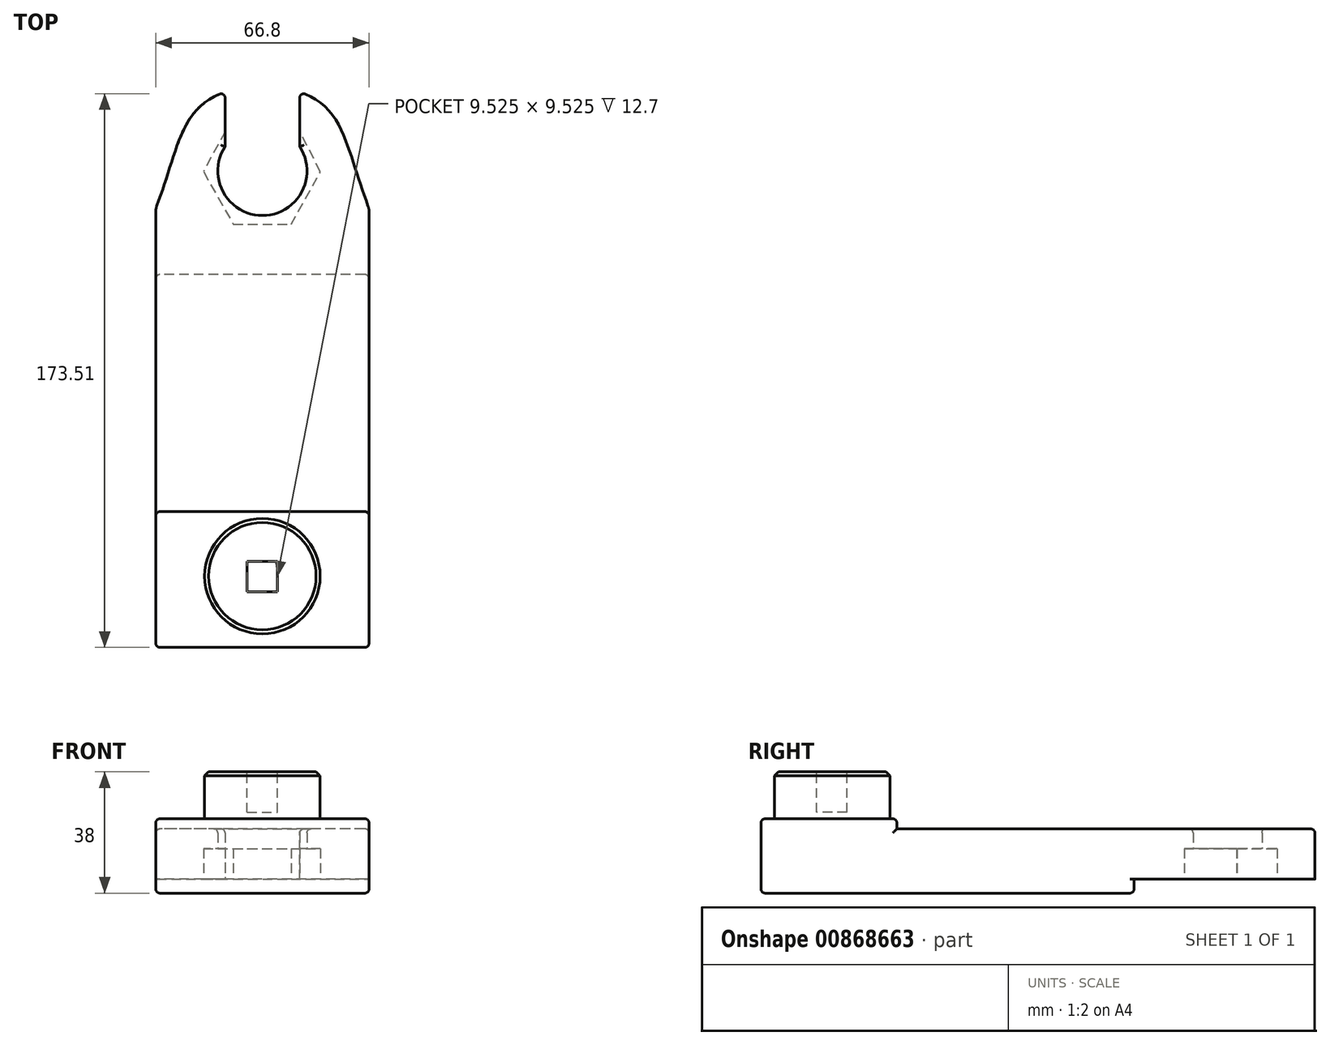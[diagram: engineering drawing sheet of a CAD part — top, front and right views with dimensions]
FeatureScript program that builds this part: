
annotation { "Feature Type Name" : "Feature", "Feature Type Description" : "" }
export const myFeature = defineFeature(function(context is Context, id is Id, definition is map)
    precondition{}
    {
        {
            var Q0;
            Q0=qCreatedBy(makeId("Top.planeOp"),FACE);
            var sketch = newSketch(context, id + "F0", { "sketchPlane" : qUnion([Q0])});
            skPoint(sketch, "E0", {"position": v(-184.46, 218.06) * mm});
            skPoint(sketch, "E1", {"position": v(-161.09, 218.06) * mm});
            skLineSegment(sketch, "E2", {"start": v(-139.37, 181.48) * mm, "end": v(-139.37, 43.95) * mm});
            skLineSegment(sketch, "E3", {"start": v(-139.37, 43.95) * mm, "end": v(-206.17, 43.95) * mm});
            skLineSegment(sketch, "E4", {"start": v(-206.17, 43.95) * mm, "end": v(-206.17, 181.48) * mm});
            skArc(sketch, "E5", {"start": v(-184.46, 200.95) * mm, "mid": v(-172.77, 179.32) * mm, "end": v(-161.09, 200.95) * mm});
            skFitSpline(sketch, "E6", {"points": [v(-206.17, 181.48) * mm, v(-184.46, 218.06) * mm], "startDerivative": vector(22.63, 60.05) * mm, "endDerivative": vector(42.75, 15.43) * mm});
            skFitSpline(sketch, "E7", {"points": [v(-161.09, 218.06) * mm, v(-139.37, 181.48) * mm], "startDerivative": vector(42.75, -15.43) * mm, "endDerivative": vector(22.63, -60.05) * mm});
            skLineSegment(sketch, "E8", {"start": v(-184.46, 218.06) * mm, "end": v(-184.46, 200.95) * mm});
            skLineSegment(sketch, "E9", {"start": v(-161.09, 218.06) * mm, "end": v(-161.09, 200.95) * mm});
            skPoint(sketch, "E10", {"position": v(-90.29, 157.9) * mm});
            skPoint(sketch, "E11", {"position": v(-85.92, 163.6) * mm});
            skSolve(sketch);
        }
        {
            var Q0;
            Q0 = qSketchRegion(id + "F0", true);
            extrude(context, id + "F1", {"entities" : qUnion([Q0]), "depth" : 15.75 * mm, "offsetDistance" : 25.4 * mm});
        }
        {
            var Q0;
            Q0=makeQuery(id+"F0.imprint","IMPRINT",FACE,{"disambiguationData":[TD([[makeQuery(id+"F0.imprint","IMPRINT",EDGE,{"derivedFrom":sQuery(id+"F0.wireOp",EDGE,"E2")}),-1.0]])]});
            var sketch = newSketch(context, id + "F2", { "sketchPlane" : qUnion([Q0])});
            skPoint(sketch, "E12", {"position": v(-88.57, 160.8) * mm});
            skLineSegment(sketch, "E13", {"start": v(-139.37, 160.8) * mm, "end": v(-206.17, 160.8) * mm});
            skLineSegment(sketch, "E14", {"start": v(-139.37, 160.8) * mm, "end": v(-139.37, 43.95) * mm});
            skLineSegment(sketch, "E15", {"start": v(-139.37, 43.95) * mm, "end": v(-206.17, 43.95) * mm});
            skLineSegment(sketch, "E16", {"start": v(-206.17, 43.95) * mm, "end": v(-206.17, 160.8) * mm});
            skSolve(sketch);
        }
        {
            var Q0;
            Q0 = qSketchRegion(id + "F2", true);
            extrude(context, id + "F3", {"entities" : qUnion([Q0]), "operationType" : NewBodyOperationType.ADD, "oppositeDirection" : true, "depth" : 4.37 * mm, "offsetDistance" : 25.4 * mm});
        }
        {
            var Q0;
            Q0=qCreatedBy(makeId("Top.planeOp"),FACE);
            var sketch = newSketch(context, id + "F4", { "sketchPlane" : qUnion([Q0])});
            skPoint(sketch, "E17", {"position": v(-71.18, 90.96) * mm});
            skPoint(sketch, "E18", {"position": v(-68, 82.73) * mm});
            skLineSegment(sketch, "E19.bottom", {"start": v(-206.17, 43.95) * mm, "end": v(-139.37, 43.95) * mm});
            skLineSegment(sketch, "E19.top", {"start": v(-206.17, 86.5) * mm, "end": v(-139.37, 86.5) * mm});
            skLineSegment(sketch, "E19.left", {"start": v(-206.17, 43.95) * mm, "end": v(-206.17, 86.5) * mm});
            skLineSegment(sketch, "E19.right", {"start": v(-139.37, 43.95) * mm, "end": v(-139.37, 86.5) * mm});
            skSolve(sketch);
        }
        {
            var Q0;
            Q0 = qSketchRegion(id + "F4", true);
            extrude(context, id + "F5", {"entities" : qUnion([Q0]), "operationType" : NewBodyOperationType.ADD, "depth" : 18.92 * mm, "offsetDistance" : 25.4 * mm});
        }
        {
            var Q0;
            Q0=makeQuery(id+"F5.opExtrude","CAP_FACE",FACE,{"disambiguationData":[OSD([sQuery(id+"F4.wireOp",EDGE,"E19.bottom"),sQuery(id+"F4.wireOp",EDGE,"E19.top"),sQuery(id+"F4.wireOp",EDGE,"E19.left"),sQuery(id+"F4.wireOp",EDGE,"E19.right")])],"isStart":false});
            var sketch = newSketch(context, id + "F6", { "sketchPlane" : qUnion([Q0])});
            skCircle(sketch, "E20", {"center": v(-172.77, 66.3) * mm, "radius": 18.1 * mm});
            skPoint(sketch, "E21", {"position": v(-67.78, 52.1) * mm});
            skPoint(sketch, "E22", {"position": v(-53.08, 52.79) * mm});
            skSolve(sketch);
        }
        {
            var Q0;
            Q0 = qSketchRegion(id + "F6", true);
            extrude(context, id + "F7", {"entities" : qUnion([Q0]), "operationType" : NewBodyOperationType.ADD, "depth" : 14.7 * mm, "offsetDistance" : 25.4 * mm});
        }
        {
            var Q0;
            Q0=makeQuery(id+"F7.opExtrude","CAP_FACE",FACE,{"disambiguationData":[OSD([sQuery(id+"F6.wireOp",EDGE,"E20")])],"isStart":false});
            var sketch = newSketch(context, id + "F8", { "sketchPlane" : qUnion([Q0])});
            skLineSegment(sketch, "E23.bottom", {"start": v(-177.53, 70.87) * mm, "end": v(-168, 70.87) * mm});
            skLineSegment(sketch, "E23.top", {"start": v(-177.53, 61.35) * mm, "end": v(-168, 61.35) * mm});
            skLineSegment(sketch, "E23.left", {"start": v(-177.53, 70.87) * mm, "end": v(-177.53, 61.35) * mm});
            skLineSegment(sketch, "E23.right", {"start": v(-168, 70.87) * mm, "end": v(-168, 61.35) * mm});
            skSolve(sketch);
        }
        {
            var Q0;
            Q0 = qSketchRegion(id + "F8", true);
            extrude(context, id + "F9", {"entities" : qUnion([Q0]), "operationType" : NewBodyOperationType.REMOVE, "oppositeDirection" : true, "depth" : 12.7 * mm, "offsetDistance" : 25.4 * mm});
        }
        {
            var Q0;
            Q0=makeQuery(id+"F1.opExtrude","SWEPT_EDGE",EDGE,{"disambiguationData":[OSD([sQuery(id+"F0.wireOp",EDGE,"E6"),sQuery(id+"F0.wireOp",EDGE,"E8")])]});
            var Q1;
            Q1=makeQuery(id+"F1.opExtrude","SWEPT_EDGE",EDGE,{"disambiguationData":[OSD([sQuery(id+"F0.wireOp",EDGE,"E7"),sQuery(id+"F0.wireOp",EDGE,"E9")])]});
            fillet(context, id + "F10", {"entities" : qUnion([Q0, Q1]), "radius" : 1.27 * mm, "tangentPropagation" : true, "allowEdgeOverflow" : false});
        }
        {
            var Q0;
            Q0=makeQuery(id+"F1.opExtrude","SWEPT_EDGE",EDGE,{"disambiguationData":[OSD([sQuery(id+"F0.wireOp",EDGE,"E2"),sQuery(id+"F0.wireOp",EDGE,"E7")])]});
            var Q1;
            Q1=makeQuery(id+"F1.opExtrude","SWEPT_EDGE",EDGE,{"disambiguationData":[OSD([sQuery(id+"F0.wireOp",EDGE,"E4"),sQuery(id+"F0.wireOp",EDGE,"E6")])]});
            fillet(context, id + "F11", {"entities" : qUnion([Q0, Q1]), "radius" : 5.08 * mm, "tangentPropagation" : true, "allowEdgeOverflow" : false});
        }
        {
            var Q0;
            Q0=makeQuery(id+"F3.opExtrude","SWEPT_EDGE",EDGE,{"disambiguationData":[OSD([sQuery(id+"F0.wireOp",EDGE,"E4"),sQuery(id+"F2.wireOp",EDGE,"E13"),sQuery(id+"F2.wireOp",EDGE,"E16")])]});
            var Q1;
            Q1=makeQuery(id+"F3.opExtrude","SWEPT_EDGE",EDGE,{"disambiguationData":[OSD([sQuery(id+"F0.wireOp",EDGE,"E2"),sQuery(id+"F2.wireOp",EDGE,"E13"),sQuery(id+"F2.wireOp",EDGE,"E14")])]});
            fillet(context, id + "F12", {"entities" : qUnion([Q0, Q1]), "radius" : 1.27 * mm, "tangentPropagation" : true, "allowEdgeOverflow" : false});
        }
        {
            var Q0;
            Q0=makeQuery(id+"F3.opExtrude","CAP_EDGE",EDGE,{"disambiguationData":[OSD([sQuery(id+"F2.wireOp",EDGE,"E13")])],"isStart":true});
            var Q1;
            Q1=makeQuery(id+"F3.opExtrude","CAP_EDGE",EDGE,{"disambiguationData":[OSD([sQuery(id+"F2.wireOp",EDGE,"E13")])],"isStart":false});
            fillet(context, id + "F13", {"entities" : qUnion([Q0, Q1]), "radius" : 1.27 * mm, "tangentPropagation" : true, "allowEdgeOverflow" : false});
        }
        {
            var Q0;
            Q0=makeQuery(id+"F5.boolean.opBoolean","MERGE",EDGE,{"derivedFrom":[makeQuery(id+"F3.boolean.opBoolean","MERGE",EDGE,{"derivedFrom":[makeQuery(id+"F1.opExtrude","SWEPT_EDGE",EDGE,{"disambiguationData":[OSD([sQuery(id+"F0.wireOp",EDGE,"E3"),sQuery(id+"F0.wireOp",EDGE,"E4")])]}),makeQuery(id+"F3.opExtrude","SWEPT_EDGE",EDGE,{"disambiguationData":[OSD([sQuery(id+"F2.wireOp",EDGE,"E15"),sQuery(id+"F2.wireOp",EDGE,"E16")])]})]}),makeQuery(id+"F5.opExtrude","SWEPT_EDGE",EDGE,{"disambiguationData":[OSD([sQuery(id+"F4.wireOp",EDGE,"E19.bottom"),sQuery(id+"F4.wireOp",EDGE,"E19.left")])]})]});
            var Q1;
            Q1=makeQuery(id+"F5.boolean.opBoolean","MERGE",EDGE,{"derivedFrom":[makeQuery(id+"F3.boolean.opBoolean","MERGE",EDGE,{"derivedFrom":[makeQuery(id+"F1.opExtrude","SWEPT_EDGE",EDGE,{"disambiguationData":[OSD([sQuery(id+"F0.wireOp",EDGE,"E2"),sQuery(id+"F0.wireOp",EDGE,"E3")])]}),makeQuery(id+"F3.opExtrude","SWEPT_EDGE",EDGE,{"disambiguationData":[OSD([sQuery(id+"F2.wireOp",EDGE,"E14"),sQuery(id+"F2.wireOp",EDGE,"E15")])]})]}),makeQuery(id+"F5.opExtrude","SWEPT_EDGE",EDGE,{"disambiguationData":[OSD([sQuery(id+"F4.wireOp",EDGE,"E19.bottom"),sQuery(id+"F4.wireOp",EDGE,"E19.right")])]})]});
            var Q2;
            Q2=makeQuery(id+"F5.opExtrude","SWEPT_EDGE",EDGE,{"disambiguationData":[OSD([sQuery(id+"F4.wireOp",EDGE,"E19.top"),sQuery(id+"F4.wireOp",EDGE,"E19.left")])]});
            var Q3;
            Q3=makeQuery(id+"F5.opExtrude","SWEPT_EDGE",EDGE,{"disambiguationData":[OSD([sQuery(id+"F4.wireOp",EDGE,"E19.top"),sQuery(id+"F4.wireOp",EDGE,"E19.right")])]});
            fillet(context, id + "F14", {"entities" : qUnion([Q0, Q1, Q2, Q3]), "radius" : 1.27 * mm, "tangentPropagation" : true, "allowEdgeOverflow" : false});
        }
        {
            var Q0;
            Q0=makeQuery(id+"F9.boolean.opBoolean","COPY",EDGE,{"derivedFrom":makeQuery(id+"F9.opExtrude","CAP_EDGE",EDGE,{"disambiguationData":[OSD([sQuery(id+"F8.wireOp",EDGE,"E23.bottom")])],"isStart":true})});
            var Q1;
            Q1=makeQuery(id+"F9.boolean.opBoolean","COPY",EDGE,{"derivedFrom":makeQuery(id+"F9.opExtrude","CAP_EDGE",EDGE,{"disambiguationData":[OSD([sQuery(id+"F8.wireOp",EDGE,"E23.right")])],"isStart":true})});
            var Q2;
            Q2=makeQuery(id+"F9.boolean.opBoolean","COPY",EDGE,{"derivedFrom":makeQuery(id+"F9.opExtrude","CAP_EDGE",EDGE,{"disambiguationData":[OSD([sQuery(id+"F8.wireOp",EDGE,"E23.top")])],"isStart":true})});
            var Q3;
            Q3=makeQuery(id+"F9.boolean.opBoolean","COPY",EDGE,{"derivedFrom":makeQuery(id+"F9.opExtrude","CAP_EDGE",EDGE,{"disambiguationData":[OSD([sQuery(id+"F8.wireOp",EDGE,"E23.left")])],"isStart":true})});
            var Q4;
            Q4=makeQuery(id+"F7.opExtrude","CAP_EDGE",EDGE,{"disambiguationData":[OSD([sQuery(id+"F6.wireOp",EDGE,"E20")])],"isStart":false});
            chamfer(context, id + "F15", {"entities" : qUnion([Q0, Q1, Q2, Q3, Q4]), "width" : 1.27 * mm, "tangentPropagation" : true});
        }
        {
            var Q0;
            Q0=makeQuery(id+"F1.opExtrude","CAP_EDGE",EDGE,{"disambiguationData":[OSD([sQuery(id+"F0.wireOp",EDGE,"E4")])],"isStart":false});
            var Q1;
            Q1=makeQuery(id+"F1.opExtrude","CAP_EDGE",EDGE,{"disambiguationData":[OSD([sQuery(id+"F0.wireOp",EDGE,"E5")])],"isStart":false});
            var Q2;
            Q2=makeQuery(id+"F1.opExtrude","CAP_EDGE",EDGE,{"disambiguationData":[OSD([sQuery(id+"F0.wireOp",EDGE,"E9")])],"isStart":false});
            fillet(context, id + "F16", {"entities" : qUnion([Q0, Q1, Q2]), "radius" : 1.27 * mm, "tangentPropagation" : true, "allowEdgeOverflow" : false});
        }
        {
            var Q0;
            Q0=makeQuery(id+"F5.opExtrude","CAP_EDGE",EDGE,{"disambiguationData":[OSD([sQuery(id+"F4.wireOp",EDGE,"E19.right")])],"isStart":false});
            fillet(context, id + "F17", {"entities" : qUnion([Q0]), "radius" : 1.27 * mm, "tangentPropagation" : true, "allowEdgeOverflow" : false});
        }
        {
            var Q0;
            Q0=makeQuery(id+"F0.imprint","IMPRINT",FACE,{"disambiguationData":[TD([[makeQuery(id+"F0.imprint","IMPRINT",EDGE,{"derivedFrom":sQuery(id+"F0.wireOp",EDGE,"E2")}),-1.0]])]});
            var sketch = newSketch(context, id + "F18", { "sketchPlane" : qUnion([Q0])});
            skLineSegment(sketch, "E24", {"start": v(-184.46, 205.6) * mm, "end": v(-191.21, 193.08) * mm});
            skLineSegment(sketch, "E25", {"start": v(-191.21, 193.08) * mm, "end": v(-181.87, 176.54) * mm});
            skLineSegment(sketch, "E26", {"start": v(-181.87, 176.54) * mm, "end": v(-163.78, 176.54) * mm});
            skLineSegment(sketch, "E27", {"start": v(-163.78, 176.54) * mm, "end": v(-154.57, 193) * mm});
            skLineSegment(sketch, "E28", {"start": v(-154.57, 193) * mm, "end": v(-161.09, 205.6) * mm});
            skArc(sketch, "E29", {"start": v(-184.46, 200.95) * mm, "mid": v(-172.77, 179.58) * mm, "end": v(-161.09, 200.95) * mm});
            skLineSegment(sketch, "E30", {"start": v(-161.09, 205.6) * mm, "end": v(-161.09, 200.95) * mm});
            skLineSegment(sketch, "E31", {"start": v(-184.46, 205.6) * mm, "end": v(-184.46, 200.95) * mm});
            skSolve(sketch);
        }
        {
            var Q0;
            Q0 = qSketchRegion(id + "F18", true);
            extrude(context, id + "F19", {"entities" : qUnion([Q0]), "operationType" : NewBodyOperationType.REMOVE, "depth" : 9.52 * mm, "offsetDistance" : 25.4 * mm});
        }
    });
